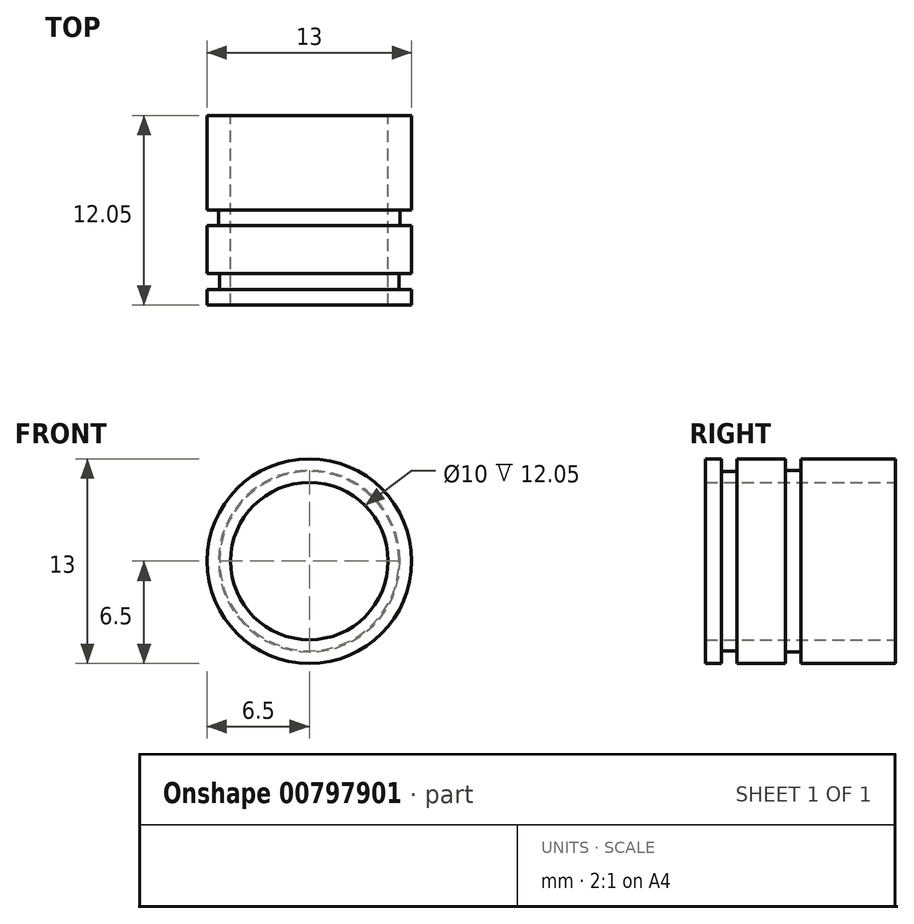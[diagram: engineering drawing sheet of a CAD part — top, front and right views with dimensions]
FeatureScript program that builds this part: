
annotation { "Feature Type Name" : "Feature", "Feature Type Description" : "" }
export const myFeature = defineFeature(function(context is Context, id is Id, definition is map)
    precondition{}
    {
        {
            var Q0;
            Q0=qCreatedBy(makeId("Front.planeOp"),FACE);
            var sketch = newSketch(context, id + "F0", { "sketchPlane" : qUnion([Q0])});
            skCircle(sketch, "E0", {"center": v(0, 0) * mm, "radius": 6.5 * mm});
            skCircle(sketch, "E1", {"center": v(0, 0) * mm, "radius": 5 * mm});
            skSolve(sketch);
        }
        {
            var Q0;
            Q0 = qSketchRegion(id + "F0", true);
            extrude(context, id + "F1", {"entities" : qUnion([Q0]), "depth" : 6 * mm, "offsetDistance" : 25 * mm});
        }
        {
            var Q0;
            Q0=makeQuery(id+"F1.opExtrude","CAP_FACE",FACE,{"disambiguationData":[OSD([sQuery(id+"F0.wireOp",EDGE,"E0"),sQuery(id+"F0.wireOp",EDGE,"E1")])],"isStart":false});
            var sketch = newSketch(context, id + "F2", { "sketchPlane" : qUnion([Q0])});
            skCircle(sketch, "E2", {"center": v(0, 0) * mm, "radius": 5 * mm});
            skCircle(sketch, "E3", {"center": v(0, 0) * mm, "radius": 5.76 * mm});
            skSolve(sketch);
        }
        {
            var Q0;
            Q0 = qSketchRegion(id + "F2", true);
            extrude(context, id + "F3", {"entities" : qUnion([Q0]), "operationType" : NewBodyOperationType.ADD, "depth" : 1 * mm, "offsetDistance" : 25 * mm});
        }
        {
            var Q0;
            Q0=makeQuery(id+"F3.opExtrude","CAP_FACE",FACE,{"disambiguationData":[OSD([sQuery(id+"F2.wireOp",EDGE,"E2"),sQuery(id+"F2.wireOp",EDGE,"E3")])],"isStart":false});
            var sketch = newSketch(context, id + "F4", { "sketchPlane" : qUnion([Q0])});
            skCircle(sketch, "E4", {"center": v(0, 0) * mm, "radius": 5 * mm});
            skCircle(sketch, "E5", {"center": v(0, 0) * mm, "radius": 6.5 * mm});
            skSolve(sketch);
        }
        {
            var Q0;
            Q0 = qSketchRegion(id + "F4", true);
            extrude(context, id + "F5", {"entities" : qUnion([Q0]), "operationType" : NewBodyOperationType.ADD, "depth" : 3.05 * mm, "offsetDistance" : 25 * mm});
        }
        {
            var Q0;
            Q0=makeQuery(id+"F5.opExtrude","CAP_FACE",FACE,{"disambiguationData":[OSD([sQuery(id+"F4.wireOp",EDGE,"E4"),sQuery(id+"F4.wireOp",EDGE,"E5")])],"isStart":false});
            var sketch = newSketch(context, id + "F6", { "sketchPlane" : qUnion([Q0])});
            skCircle(sketch, "E6", {"center": v(0, 0) * mm, "radius": 5 * mm});
            skCircle(sketch, "E7", {"center": v(0, 0) * mm, "radius": 5.7 * mm});
            skSolve(sketch);
        }
        {
            var Q0;
            Q0 = qSketchRegion(id + "F6", true);
            extrude(context, id + "F7", {"entities" : qUnion([Q0]), "operationType" : NewBodyOperationType.ADD, "depth" : 1 * mm, "offsetDistance" : 25 * mm});
        }
        {
            var Q0;
            Q0=makeQuery(id+"F7.opExtrude","CAP_FACE",FACE,{"disambiguationData":[OSD([sQuery(id+"F6.wireOp",EDGE,"E6"),sQuery(id+"F6.wireOp",EDGE,"E7")])],"isStart":false});
            var sketch = newSketch(context, id + "F8", { "sketchPlane" : qUnion([Q0])});
            skCircle(sketch, "E8", {"center": v(0, 0) * mm, "radius": 5 * mm});
            skCircle(sketch, "E9", {"center": v(0, 0) * mm, "radius": 6.5 * mm});
            skSolve(sketch);
        }
        {
            var Q0;
            Q0 = qSketchRegion(id + "F8", true);
            extrude(context, id + "F9", {"entities" : qUnion([Q0]), "operationType" : NewBodyOperationType.ADD, "depth" : 1 * mm, "offsetDistance" : 25 * mm});
        }
    });
